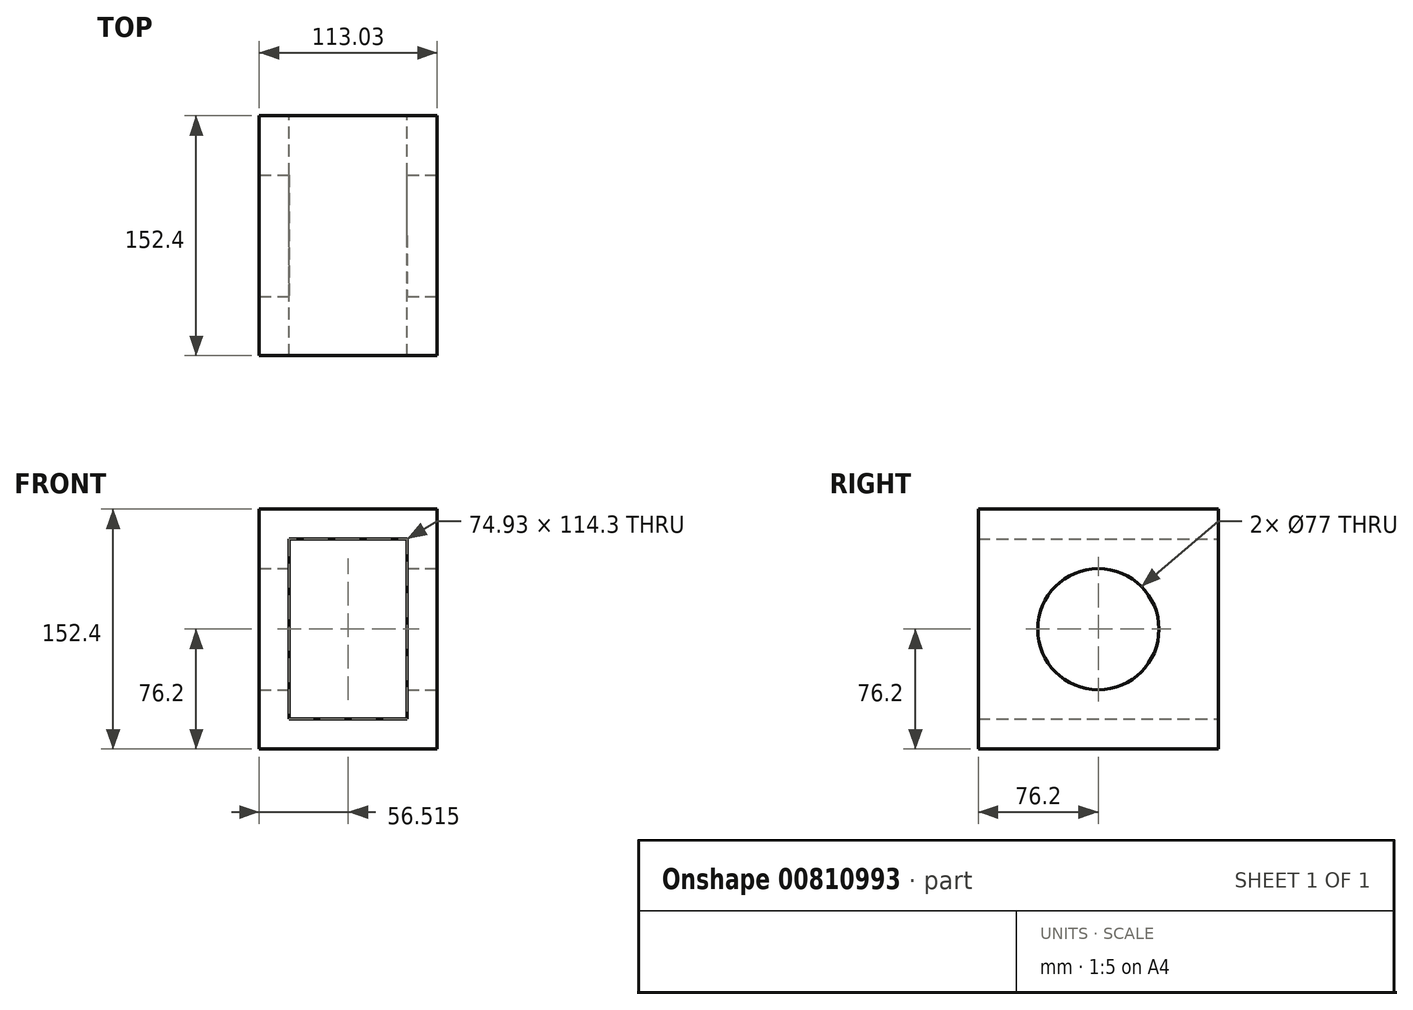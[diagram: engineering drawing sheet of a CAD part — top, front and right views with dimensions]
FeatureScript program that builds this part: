
annotation { "Feature Type Name" : "Feature", "Feature Type Description" : "" }
export const myFeature = defineFeature(function(context is Context, id is Id, definition is map)
    precondition{}
    {
        {
            var Q0;
            Q0=qCreatedBy(makeId("Front.planeOp"),FACE);
            var sketch = newSketch(context, id + "F0", { "sketchPlane" : qUnion([Q0])});
            skLineSegment(sketch, "E0.bottom", {"start": v(0, 0) * mm, "end": v(113.03, 0) * mm});
            skLineSegment(sketch, "E0.top", {"start": v(0, 152.4) * mm, "end": v(113.03, 152.4) * mm});
            skLineSegment(sketch, "E0.left", {"start": v(0, 0) * mm, "end": v(0, 152.4) * mm});
            skLineSegment(sketch, "E0.right", {"start": v(113.03, 0) * mm, "end": v(113.03, 152.4) * mm});
            skLineSegment(sketch, "E1.0", {"start": v(19.05, 19.05) * mm, "end": v(19.05, 133.35) * mm});
            skLineSegment(sketch, "E1.1", {"start": v(19.05, 19.05) * mm, "end": v(93.98, 19.05) * mm});
            skLineSegment(sketch, "E1.2", {"start": v(93.98, 19.05) * mm, "end": v(93.98, 133.35) * mm});
            skLineSegment(sketch, "E1.3", {"start": v(19.05, 133.35) * mm, "end": v(93.98, 133.35) * mm});
            skSolve(sketch);
        }
        {
            var Q0;
            Q0 = qSketchRegion(id + "F0", true);
            extrude(context, id + "F1", {"entities" : qUnion([Q0]), "depth" : 152.4 * mm, "offsetDistance" : 25.4 * mm});
        }
        {
            var Q0;
            Q0=makeQuery(id+"F1.opExtrude","SWEPT_FACE",FACE,{"disambiguationData":[OSD([sQuery(id+"F0.wireOp",EDGE,"E0.right")])]});
            var sketch = newSketch(context, id + "F2", { "sketchPlane" : qUnion([Q0])});
            skLineSegment(sketch, "E2", {"start": v(0, 152.4) * mm, "end": v(-152.4, 0) * mm});
            skCircle(sketch, "E3", {"center": v(-76.2, 76.2) * mm, "radius": 38.5 * mm});
            skSolve(sketch);
        }
        {
            var Q0;
            Q0 = qSketchRegion(id + "F2", true);
            extrude(context, id + "F3", {"entities" : qUnion([Q0]), "operationType" : NewBodyOperationType.REMOVE, "endBound" : BoundingType.THROUGH_ALL, "oppositeDirection" : true, "depth" : 25.4 * mm, "offsetDistance" : 25.4 * mm});
        }
    });
